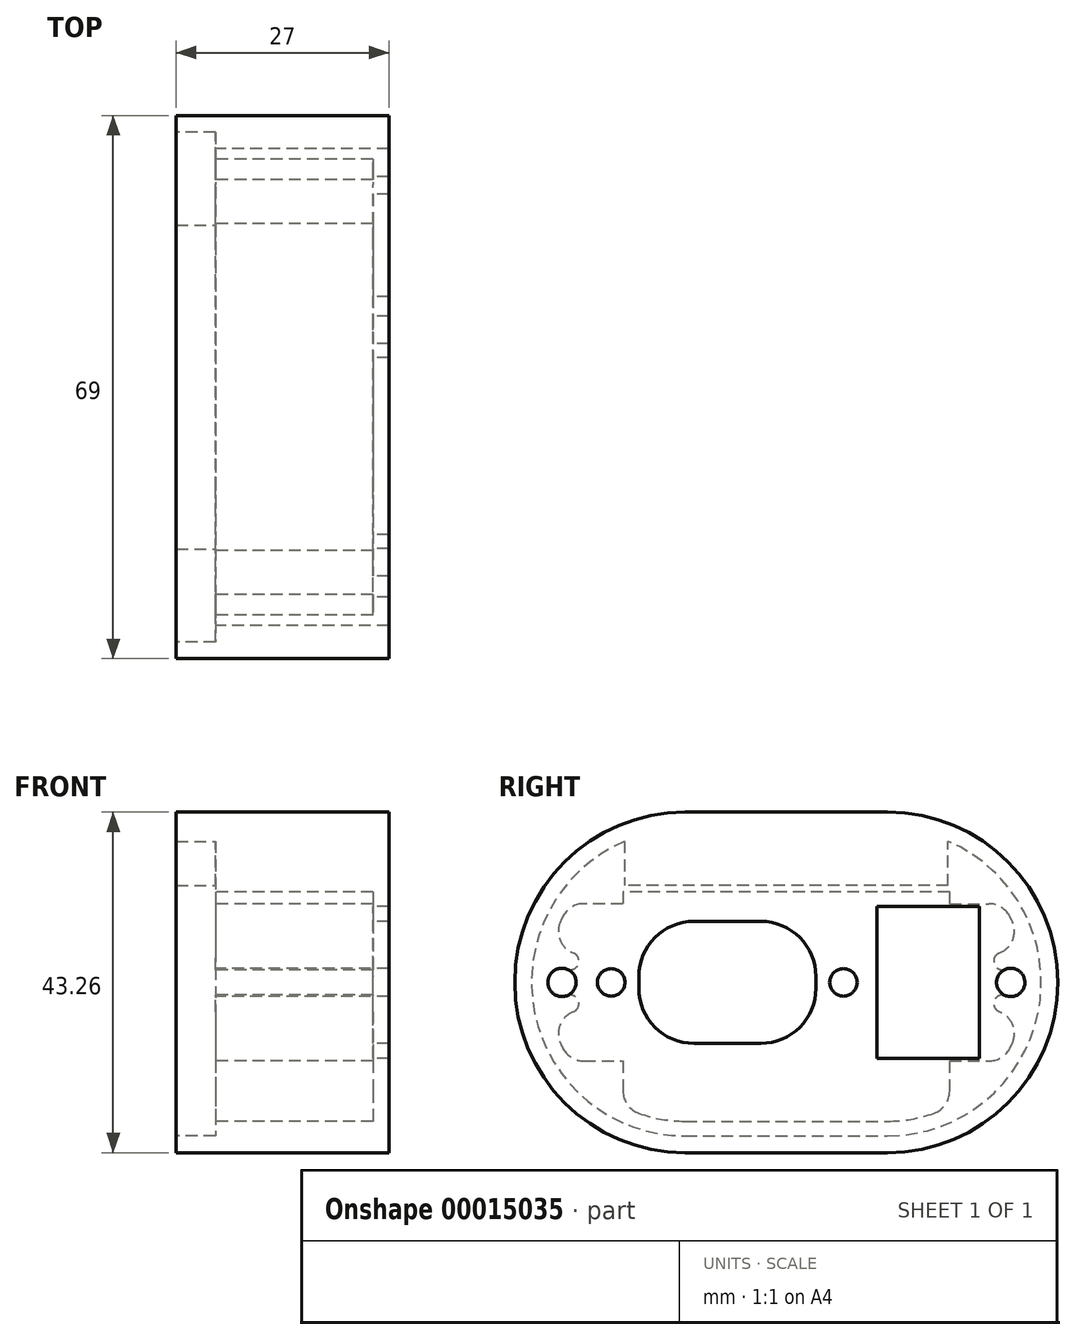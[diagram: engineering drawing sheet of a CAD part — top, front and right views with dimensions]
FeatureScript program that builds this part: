
annotation { "Feature Type Name" : "Feature", "Feature Type Description" : "" }
export const myFeature = defineFeature(function(context is Context, id is Id, definition is map)
    precondition{}
    {
        {
            var Q0;
            Q0=qCreatedBy(makeId("Right.planeOp"),FACE);
            var sketch = newSketch(context, id + "F0", { "sketchPlane" : qUnion([Q0])});
            skLineSegment(sketch, "E0.rect.bottom", {"start": v(23.75, -10) * mm, "end": v(-23.75, -10) * mm});
            skLineSegment(sketch, "E0.rect.top", {"start": v(23.75, 10) * mm, "end": v(-23.75, 10) * mm});
            skLineSegment(sketch, "E0.rect.left", {"start": v(23.75, -10) * mm, "end": v(23.75, 10) * mm});
            skLineSegment(sketch, "E0.rect.right", {"start": v(-23.75, -10) * mm, "end": v(-23.75, 10) * mm});
            skLineSegment(sketch, "E1.bottom", {"start": v(-23.75, 10) * mm, "end": v(23.75, 10) * mm});
            skLineSegment(sketch, "E1.top", {"start": v(-23.75, 12.1) * mm, "end": v(23.75, 12.1) * mm});
            skLineSegment(sketch, "E1.left", {"start": v(-23.75, 10) * mm, "end": v(-23.75, 12.1) * mm});
            skLineSegment(sketch, "E1.right", {"start": v(23.75, 10) * mm, "end": v(23.75, 12.1) * mm});
            skLineSegment(sketch, "E2.bottom", {"start": v(-23.75, -10) * mm, "end": v(23.75, -10) * mm});
            skLineSegment(sketch, "E2.top", {"start": v(-23.75, -12.1) * mm, "end": v(23.75, -12.1) * mm});
            skLineSegment(sketch, "E2.left", {"start": v(-23.75, -10) * mm, "end": v(-23.75, -12.1) * mm});
            skLineSegment(sketch, "E2.right", {"start": v(23.75, -10) * mm, "end": v(23.75, -12.1) * mm});
            skLineSegment(sketch, "E3", {"start": v(-23.75, 10) * mm, "end": v(0, 0) * mm, "construction": true});
            skLineSegment(sketch, "E4", {"start": v(0, 0) * mm, "end": v(23.75, -10) * mm, "construction": true});
            skLineSegment(sketch, "E5", {"start": v(-23.75, -10) * mm, "end": v(-20.75, -10) * mm});
            skLineSegment(sketch, "E6", {"start": v(-20.75, -10) * mm, "end": v(-20.75, -8) * mm});
            skLineSegment(sketch, "E7", {"start": v(-20.75, -8) * mm, "end": v(-25.75, -8) * mm});
            skLineSegment(sketch, "E8", {"start": v(-25.75, -8) * mm, "end": v(-25.75, -14.1) * mm});
            skLineSegment(sketch, "E9", {"start": v(-25.75, -14.1) * mm, "end": v(-20.75, -14.1) * mm});
            skLineSegment(sketch, "E10", {"start": v(-20.75, -14.1) * mm, "end": v(-20.75, -17.1) * mm});
            skLineSegment(sketch, "E11", {"start": v(-20.75, -17.1) * mm, "end": v(20.75, -17.1) * mm});
            skLineSegment(sketch, "E12", {"start": v(20.75, -17.1) * mm, "end": v(20.75, -14.1) * mm});
            skLineSegment(sketch, "E13", {"start": v(20.75, -14.1) * mm, "end": v(25.75, -14.1) * mm});
            skLineSegment(sketch, "E14", {"start": v(25.75, -14.1) * mm, "end": v(25.75, -8) * mm});
            skLineSegment(sketch, "E15", {"start": v(25.75, -8) * mm, "end": v(20.75, -8) * mm});
            skLineSegment(sketch, "E16", {"start": v(20.75, -8) * mm, "end": v(20.75, -10) * mm});
            skLineSegment(sketch, "E17", {"start": v(-20.75, 10) * mm, "end": v(-20.75, 8) * mm});
            skLineSegment(sketch, "E18", {"start": v(-20.75, 8) * mm, "end": v(-25.75, 8) * mm});
            skLineSegment(sketch, "E19", {"start": v(-25.75, 8) * mm, "end": v(-25.75, 14.1) * mm});
            skLineSegment(sketch, "E20", {"start": v(-25.75, 14.1) * mm, "end": v(-20.75, 14.1) * mm});
            skLineSegment(sketch, "E21", {"start": v(-20.75, 14.1) * mm, "end": v(-20.75, 12.1) * mm});
            skLineSegment(sketch, "E22", {"start": v(20.75, 12.1) * mm, "end": v(20.75, 14.1) * mm});
            skLineSegment(sketch, "E23", {"start": v(20.75, 14.1) * mm, "end": v(25.75, 14.1) * mm});
            skLineSegment(sketch, "E24", {"start": v(25.75, 14.1) * mm, "end": v(25.75, 8) * mm});
            skLineSegment(sketch, "E25", {"start": v(25.75, 8) * mm, "end": v(20.75, 8) * mm});
            skLineSegment(sketch, "E26", {"start": v(20.75, 8) * mm, "end": v(20.75, 10) * mm});
            skCircle(sketch, "E27", {"center": v(-28.5, 0) * mm, "radius": 1.25 * mm});
            skCircle(sketch, "E28", {"center": v(28.5, 0) * mm, "radius": 1.25 * mm});
            skLineSegment(sketch, "E29", {"start": v(-28.5, 0) * mm, "end": v(0, 0) * mm, "construction": true});
            skLineSegment(sketch, "E30", {"start": v(28.5, 0) * mm, "end": v(0, 0) * mm, "construction": true});
            skLineSegment(sketch, "E31.bottom", {"start": v(-25.75, -14.1) * mm, "end": v(25.75, -14.1) * mm});
            skLineSegment(sketch, "E31.top", {"start": v(-25.75, -19.1) * mm, "end": v(25.75, -19.1) * mm});
            skLineSegment(sketch, "E31.left", {"start": v(-25.75, -14.1) * mm, "end": v(-25.75, -19.1) * mm});
            skLineSegment(sketch, "E31.right", {"start": v(25.75, -14.1) * mm, "end": v(25.75, -19.1) * mm});
            skArc(sketch, "E32", {"start": v(-12.87, 19.1) * mm, "mid": v(-31.97, 0) * mm, "end": v(-12.87, -19.1) * mm});
            skArc(sketch, "E33", {"start": v(12.87, -19.1) * mm, "mid": v(31.97, 0) * mm, "end": v(12.87, 19.1) * mm});
            skLineSegment(sketch, "E34", {"start": v(-12.87, 19.1) * mm, "end": v(-12.87, 0) * mm, "construction": true});
            skLineSegment(sketch, "E35", {"start": v(-12.87, -19.1) * mm, "end": v(-12.87, 0) * mm, "construction": true});
            skLineSegment(sketch, "E36", {"start": v(12.87, 0) * mm, "end": v(12.87, 19.1) * mm, "construction": true});
            skLineSegment(sketch, "E37", {"start": v(12.87, 0) * mm, "end": v(12.87, -19.1) * mm, "construction": true});
            skLineSegment(sketch, "E38.rect.bottom", {"start": v(24.5, -9.65) * mm, "end": v(11.5, -9.65) * mm});
            skLineSegment(sketch, "E38.rect.top", {"start": v(24.5, 9.65) * mm, "end": v(11.5, 9.65) * mm});
            skLineSegment(sketch, "E38.rect.left", {"start": v(24.5, -9.65) * mm, "end": v(24.5, 9.65) * mm});
            skLineSegment(sketch, "E38.rect.right", {"start": v(11.5, -9.65) * mm, "end": v(11.5, 9.65) * mm});
            skPoint(sketch, "E38.rect.middle", {"position": v(18, 0) * mm});
            skLineSegment(sketch, "E39.rect.bottom", {"start": v(3.75, -7.75) * mm, "end": v(-18.75, -7.75) * mm});
            skLineSegment(sketch, "E39.rect.top", {"start": v(3.75, 7.75) * mm, "end": v(-18.75, 7.75) * mm});
            skLineSegment(sketch, "E39.rect.left", {"start": v(3.75, -7.75) * mm, "end": v(3.75, 7.75) * mm});
            skLineSegment(sketch, "E39.rect.right", {"start": v(-18.75, -7.75) * mm, "end": v(-18.75, 7.75) * mm});
            skPoint(sketch, "E39.rect.middle", {"position": v(-7.5, 0) * mm});
            skCircle(sketch, "E40", {"center": v(-22.25, 0) * mm, "radius": 1.75 * mm});
            skCircle(sketch, "E41", {"center": v(7.25, 0) * mm, "radius": 1.75 * mm});
            skLineSegment(sketch, "E42", {"start": v(-22.25, 0) * mm, "end": v(-7.5, 0) * mm, "construction": true});
            skLineSegment(sketch, "E43", {"start": v(-7.5, 0) * mm, "end": v(7.25, 0) * mm, "construction": true});
            skLineSegment(sketch, "E44.rect.bottom", {"start": v(10.5, 8.5) * mm, "end": v(-25.5, 8.5) * mm});
            skLineSegment(sketch, "E44.rect.top", {"start": v(10.5, -8.5) * mm, "end": v(-25.5, -8.5) * mm});
            skLineSegment(sketch, "E44.rect.left", {"start": v(10.5, 8.5) * mm, "end": v(10.5, -8.5) * mm});
            skLineSegment(sketch, "E44.rect.right", {"start": v(-25.5, 8.5) * mm, "end": v(-25.5, -8.5) * mm});
            skLineSegment(sketch, "E45.rect.bottom", {"start": v(25.5, 10.5) * mm, "end": v(10.5, 10.5) * mm});
            skLineSegment(sketch, "E45.rect.top", {"start": v(25.5, -10.5) * mm, "end": v(10.5, -10.5) * mm});
            skLineSegment(sketch, "E45.rect.left", {"start": v(25.5, 10.5) * mm, "end": v(25.5, -10.5) * mm});
            skLineSegment(sketch, "E45.rect.right", {"start": v(10.5, 10.5) * mm, "end": v(10.5, -10.5) * mm});
            skLineSegment(sketch, "E46", {"start": v(-20.75, 14.1) * mm, "end": v(-20.75, 17.4) * mm});
            skLineSegment(sketch, "E47", {"start": v(20.75, 14.1) * mm, "end": v(20.75, 17.4) * mm});
            skSolve(sketch);
        }
        {
            var Q0;
            Q0=qCreatedBy(makeId("Right.planeOp"),FACE);
            var sketch = newSketch(context, id + "F1", { "sketchPlane" : qUnion([Q0])});
            skArc(sketch, "E48", {"start": v(-12.87, 19.5) * mm, "mid": v(-32.37, 0) * mm, "end": v(-12.87, -19.5) * mm});
            skArc(sketch, "E49", {"start": v(12.87, -19.5) * mm, "mid": v(32.37, 0) * mm, "end": v(12.87, 19.5) * mm});
            skLineSegment(sketch, "E50", {"start": v(-12.87, 19.5) * mm, "end": v(12.87, 19.5) * mm});
            skLineSegment(sketch, "E51", {"start": v(-12.87, -19.5) * mm, "end": v(12.87, -19.5) * mm});
            skLineSegment(sketch, "E52.0", {"start": v(-12.87, 21.63) * mm, "end": v(12.87, 21.63) * mm});
            skArc(sketch, "E52.1", {"start": v(-12.87, 21.63) * mm, "mid": v(-34.5, 0) * mm, "end": v(-12.87, -21.63) * mm});
            skLineSegment(sketch, "E52.2", {"start": v(-12.87, -21.63) * mm, "end": v(12.87, -21.63) * mm});
            skArc(sketch, "E52.3", {"start": v(12.87, -21.63) * mm, "mid": v(34.5, 0) * mm, "end": v(12.87, 21.63) * mm});
            skPoint(sketch, "E53", {"position": v(-34.5, 0) * mm});
            skPoint(sketch, "E54", {"position": v(34.5, 0) * mm});
            skSolve(sketch);
        }
        {
            var Q0;
            Q0 = qSketchRegion(id + "F1", true);
            extrude(context, id + "F2", {"entities" : qUnion([Q0]), "depth" : 5 * mm});
        }
        {
            var Q0;
            Q0=makeQuery(id+"F2.opExtrude","CAP_FACE",FACE,{"disambiguationData":[OSD([sQuery(id+"F1.wireOp",EDGE,"E48"),sQuery(id+"F1.wireOp",EDGE,"E49"),sQuery(id+"F1.wireOp",EDGE,"E50"),sQuery(id+"F1.wireOp",EDGE,"E51"),sQuery(id+"F1.wireOp",EDGE,"E52.0"),sQuery(id+"F1.wireOp",EDGE,"E52.1"),sQuery(id+"F1.wireOp",EDGE,"E52.2"),sQuery(id+"F1.wireOp",EDGE,"E52.3")])],"isStart":false});
            var sketch = newSketch(context, id + "F3", { "sketchPlane" : qUnion([Q0])});
            skLineSegment(sketch, "E55.0", {"start": v(-12.87, 17.63) * mm, "end": v(12.87, 17.63) * mm, "construction": true});
            skArc(sketch, "E55.1", {"start": v(-12.87, 17.63) * mm, "mid": v(-15.85, 17.38) * mm, "end": v(-18.75, 16.62) * mm, "construction": true});
            skLineSegment(sketch, "E55.2", {"start": v(-12.87, -17.63) * mm, "end": v(12.87, -17.63) * mm});
            skArc(sketch, "E55.3", {"start": v(12.87, -17.63) * mm, "mid": v(15.85, -17.38) * mm, "end": v(18.75, -16.62) * mm});
            skLineSegment(sketch, "E56.0", {"start": v(-12.87, 21.63) * mm, "end": v(12.87, 21.63) * mm});
            skArc(sketch, "E56.1", {"start": v(-12.87, 21.63) * mm, "mid": v(-34.5, 0) * mm, "end": v(-12.87, -21.63) * mm});
            skArc(sketch, "E56.2", {"start": v(12.87, -21.63) * mm, "mid": v(34.5, 0) * mm, "end": v(12.87, 21.63) * mm});
            skLineSegment(sketch, "E56.3", {"start": v(-12.87, -21.63) * mm, "end": v(12.87, -21.63) * mm});
            skArc(sketch, "E57", {"start": v(-27.85, 1.68) * mm, "mid": v(-30.3, 0) * mm, "end": v(-27.85, -1.68) * mm});
            skArc(sketch, "E58", {"start": v(27.85, -1.68) * mm, "mid": v(30.3, 0) * mm, "end": v(27.85, 1.68) * mm});
            skArc(sketch, "E59", {"start": v(27.05, 3.73) * mm, "mid": v(24.5, 0) * mm, "end": v(27.05, -3.73) * mm, "construction": true});
            skArc(sketch, "E60.trimOffspring", {"start": v(-28.65, -7.86) * mm, "mid": v(-28.5, -8.15) * mm, "end": v(-28.35, -8.44) * mm});
            skArc(sketch, "E61.trimOffspring", {"start": v(28.65, 7.86) * mm, "mid": v(28.5, 8.15) * mm, "end": v(28.35, 8.44) * mm});
            skPoint(sketch, "E62.visualSharp", {"position": v(-28.65, 7.86) * mm});
            skArc(sketch, "E62.filletArc", {"start": v(-28.65, 7.86) * mm, "mid": v(-28.76, 5.44) * mm, "end": v(-27.05, 3.73) * mm});
            skArc(sketch, "E63.filletArc", {"start": v(-27.05, -3.73) * mm, "mid": v(-28.76, -5.44) * mm, "end": v(-28.65, -7.86) * mm});
            skPoint(sketch, "E64.visualSharp", {"position": v(30.12, 3.66) * mm});
            skArc(sketch, "E64.filletArc", {"start": v(27.05, 3.73) * mm, "mid": v(28.76, 5.44) * mm, "end": v(28.65, 7.86) * mm});
            skPoint(sketch, "E65.visualSharp", {"position": v(30.12, -3.66) * mm});
            skArc(sketch, "E65.filletArc", {"start": v(28.65, -7.86) * mm, "mid": v(28.76, -5.44) * mm, "end": v(27.05, -3.73) * mm});
            skArc(sketch, "E66", {"start": v(-27.85, 1.68) * mm, "mid": v(-26.42, 2.3) * mm, "end": v(-27.05, 3.73) * mm});
            skArc(sketch, "E67", {"start": v(-27.05, -3.73) * mm, "mid": v(-26.42, -2.3) * mm, "end": v(-27.85, -1.68) * mm});
            skArc(sketch, "E68", {"start": v(27.05, 3.73) * mm, "mid": v(26.42, 2.3) * mm, "end": v(27.85, 1.68) * mm});
            skArc(sketch, "E69", {"start": v(27.85, -1.68) * mm, "mid": v(26.42, -2.3) * mm, "end": v(27.05, -3.73) * mm});
            skCircle(sketch, "E70", {"center": v(-28.5, 0) * mm, "radius": 1.8 * mm, "construction": true});
            skCircle(sketch, "E71", {"center": v(-28.5, 0) * mm, "radius": 4 * mm, "construction": true});
            skLineSegment(sketch, "E72", {"start": v(20.75, 13.8) * mm, "end": v(20.75, 10) * mm, "construction": true});
            skLineSegment(sketch, "E73", {"start": v(20.75, 10) * mm, "end": v(25.72, 10) * mm});
            skLineSegment(sketch, "E74", {"start": v(-20.75, 13.8) * mm, "end": v(-20.75, 10) * mm, "construction": true});
            skLineSegment(sketch, "E75", {"start": v(-20.75, 10) * mm, "end": v(-25.72, 10) * mm});
            skLineSegment(sketch, "E76", {"start": v(-25.72, -10) * mm, "end": v(-20.75, -10) * mm});
            skLineSegment(sketch, "E77", {"start": v(-20.75, -10) * mm, "end": v(-20.75, -13.8) * mm});
            skLineSegment(sketch, "E78", {"start": v(20.75, -13.8) * mm, "end": v(20.75, -10) * mm});
            skLineSegment(sketch, "E79", {"start": v(20.75, -10) * mm, "end": v(25.72, -10) * mm});
            skArc(sketch, "E80.trimOffspring", {"start": v(-28.35, 8.44) * mm, "mid": v(-28.5, 8.15) * mm, "end": v(-28.65, 7.86) * mm});
            skArc(sketch, "E81.trimOffspring", {"start": v(18.75, 16.62) * mm, "mid": v(15.85, 17.38) * mm, "end": v(12.87, 17.63) * mm, "construction": true});
            skArc(sketch, "E82.trimOffspring", {"start": v(28.35, -8.44) * mm, "mid": v(28.5, -8.15) * mm, "end": v(28.65, -7.86) * mm});
            skArc(sketch, "E83.trimOffspring", {"start": v(-18.75, -16.62) * mm, "mid": v(-15.85, -17.38) * mm, "end": v(-12.87, -17.63) * mm});
            skPoint(sketch, "E84.visualSharp", {"position": v(-20.75, 15.77) * mm});
            skArc(sketch, "E84.filletArc", {"start": v(-18.75, 16.62) * mm, "mid": v(-20.2, 15.53) * mm, "end": v(-20.75, 13.8) * mm, "construction": true});
            skPoint(sketch, "E85.visualSharp", {"position": v(-27.4, 10) * mm});
            skArc(sketch, "E85.filletArc", {"start": v(-25.72, 10) * mm, "mid": v(-27.25, 9.58) * mm, "end": v(-28.35, 8.44) * mm});
            skPoint(sketch, "E86.visualSharp", {"position": v(-27.4, -10) * mm});
            skArc(sketch, "E86.filletArc", {"start": v(-28.35, -8.44) * mm, "mid": v(-27.25, -9.58) * mm, "end": v(-25.72, -10) * mm});
            skPoint(sketch, "E87.visualSharp", {"position": v(-20.75, -15.77) * mm});
            skArc(sketch, "E87.filletArc", {"start": v(-20.75, -13.8) * mm, "mid": v(-20.2, -15.53) * mm, "end": v(-18.75, -16.62) * mm});
            skPoint(sketch, "E88.visualSharp", {"position": v(20.75, -15.77) * mm});
            skArc(sketch, "E88.filletArc", {"start": v(18.75, -16.62) * mm, "mid": v(20.2, -15.53) * mm, "end": v(20.75, -13.8) * mm});
            skPoint(sketch, "E89.visualSharp", {"position": v(27.4, -10) * mm});
            skArc(sketch, "E89.filletArc", {"start": v(25.72, -10) * mm, "mid": v(27.25, -9.58) * mm, "end": v(28.35, -8.44) * mm});
            skPoint(sketch, "E90.visualSharp", {"position": v(27.4, 10) * mm});
            skArc(sketch, "E90.filletArc", {"start": v(28.35, 8.44) * mm, "mid": v(27.25, 9.58) * mm, "end": v(25.72, 10) * mm});
            skPoint(sketch, "E91.visualSharp", {"position": v(20.75, 15.77) * mm});
            skArc(sketch, "E91.filletArc", {"start": v(20.75, 13.8) * mm, "mid": v(20.2, 15.53) * mm, "end": v(18.75, 16.62) * mm, "construction": true});
            skLineSegment(sketch, "E92", {"start": v(20.75, 11.5) * mm, "end": v(-20.75, 11.5) * mm});
            skLineSegment(sketch, "E93", {"start": v(-20.75, 11.5) * mm, "end": v(-20.75, 10) * mm});
            skLineSegment(sketch, "E94", {"start": v(20.75, 10) * mm, "end": v(20.75, 11.5) * mm});
            skSolve(sketch);
        }
        {
            var Q0;
            Q0 = qSketchRegion(id + "F3", true);
            extrude(context, id + "F4", {"entities" : qUnion([Q0]), "operationType" : NewBodyOperationType.ADD, "depth" : 20 * mm});
        }
        {
            var Q0;
            Q0=makeQuery(id+"F4.opExtrude","CAP_FACE",FACE,{"disambiguationData":[OSD([sQuery(id+"F3.wireOp",EDGE,"E55.0"),sQuery(id+"F3.wireOp",EDGE,"E55.1"),sQuery(id+"F3.wireOp",EDGE,"E55.2"),sQuery(id+"F3.wireOp",EDGE,"E55.3"),sQuery(id+"F3.wireOp",EDGE,"E56.0"),sQuery(id+"F3.wireOp",EDGE,"E56.1"),sQuery(id+"F3.wireOp",EDGE,"E56.2"),sQuery(id+"F3.wireOp",EDGE,"E56.3"),sQuery(id+"F3.wireOp",EDGE,"E57"),sQuery(id+"F3.wireOp",EDGE,"E58"),sQuery(id+"F3.wireOp",EDGE,"E60.trimOffspring"),sQuery(id+"F3.wireOp",EDGE,"E61.trimOffspring"),sQuery(id+"F3.wireOp",EDGE,"E62.filletArc"),sQuery(id+"F3.wireOp",EDGE,"E63.filletArc"),sQuery(id+"F3.wireOp",EDGE,"E64.filletArc"),sQuery(id+"F3.wireOp",EDGE,"E65.filletArc"),sQuery(id+"F3.wireOp",EDGE,"E66"),sQuery(id+"F3.wireOp",EDGE,"E67"),sQuery(id+"F3.wireOp",EDGE,"E68"),sQuery(id+"F3.wireOp",EDGE,"E69")])],"isStart":false});
            var sketch = newSketch(context, id + "F5", { "sketchPlane" : qUnion([Q0])});
            skLineSegment(sketch, "E95.0", {"start": v(-12.87, 21.63) * mm, "end": v(12.87, 21.63) * mm});
            skArc(sketch, "E95.1", {"start": v(-12.87, 21.63) * mm, "mid": v(-34.5, 0) * mm, "end": v(-12.87, -21.63) * mm});
            skLineSegment(sketch, "E95.2", {"start": v(-12.87, -21.63) * mm, "end": v(12.87, -21.63) * mm});
            skArc(sketch, "E95.3", {"start": v(12.87, -21.63) * mm, "mid": v(34.5, 0) * mm, "end": v(12.87, 21.63) * mm});
            skCircle(sketch, "E96.0", {"center": v(-22.25, 0) * mm, "radius": 1.75 * mm});
            skCircle(sketch, "E96.1", {"center": v(7.25, 0) * mm, "radius": 1.75 * mm});
            skLineSegment(sketch, "E97.0", {"start": v(-18.75, -0.75) * mm, "end": v(-18.75, 0.75) * mm});
            skLineSegment(sketch, "E97.1", {"start": v(-3.25, 7.75) * mm, "end": v(-11.75, 7.75) * mm});
            skLineSegment(sketch, "E97.2", {"start": v(3.75, -0.75) * mm, "end": v(3.75, 0.75) * mm});
            skLineSegment(sketch, "E97.3", {"start": v(-3.25, -7.75) * mm, "end": v(-11.75, -7.75) * mm});
            skLineSegment(sketch, "E98.0", {"start": v(11.5, -9.65) * mm, "end": v(11.5, 9.65) * mm});
            skLineSegment(sketch, "E98.1", {"start": v(24.5, 9.65) * mm, "end": v(11.5, 9.65) * mm});
            skLineSegment(sketch, "E98.2", {"start": v(24.5, -9.65) * mm, "end": v(24.5, 9.65) * mm});
            skLineSegment(sketch, "E98.3", {"start": v(24.5, -9.65) * mm, "end": v(11.5, -9.65) * mm});
            skPoint(sketch, "E99.visualSharp", {"position": v(-18.75, 7.75) * mm});
            skArc(sketch, "E99.filletArc", {"start": v(-11.75, 7.75) * mm, "mid": v(-16.7, 5.7) * mm, "end": v(-18.75, 0.75) * mm});
            skPoint(sketch, "E100.visualSharp", {"position": v(-18.75, -7.75) * mm});
            skArc(sketch, "E100.filletArc", {"start": v(-18.75, -0.75) * mm, "mid": v(-16.7, -5.7) * mm, "end": v(-11.75, -7.75) * mm});
            skPoint(sketch, "E101.visualSharp", {"position": v(3.75, 7.75) * mm});
            skArc(sketch, "E101.filletArc", {"start": v(3.75, 0.75) * mm, "mid": v(1.7, 5.7) * mm, "end": v(-3.25, 7.75) * mm});
            skPoint(sketch, "E102.visualSharp", {"position": v(3.75, -7.75) * mm});
            skArc(sketch, "E102.filletArc", {"start": v(-3.25, -7.75) * mm, "mid": v(1.7, -5.7) * mm, "end": v(3.75, -0.75) * mm});
            skCircle(sketch, "E103", {"center": v(-28.5, 0) * mm, "radius": 1.8 * mm});
            skCircle(sketch, "E104", {"center": v(28.5, 0) * mm, "radius": 1.8 * mm});
            skSolve(sketch);
        }
        {
            var Q0;
            Q0 = qSketchRegion(id + "F5", true);
            extrude(context, id + "F6", {"entities" : qUnion([Q0]), "operationType" : NewBodyOperationType.ADD, "depth" : 2 * mm});
        }
        {
            var Q0;
            Q0=makeQuery(id+"F4.opExtrude","CAP_FACE",FACE,{"disambiguationData":[OSD([sQuery(id+"F3.wireOp",EDGE,"E55.2"),sQuery(id+"F3.wireOp",EDGE,"E55.3"),sQuery(id+"F3.wireOp",EDGE,"E56.0"),sQuery(id+"F3.wireOp",EDGE,"E56.1"),sQuery(id+"F3.wireOp",EDGE,"E56.2"),sQuery(id+"F3.wireOp",EDGE,"E56.3"),sQuery(id+"F3.wireOp",EDGE,"E57"),sQuery(id+"F3.wireOp",EDGE,"E58"),sQuery(id+"F3.wireOp",EDGE,"E60.trimOffspring"),sQuery(id+"F3.wireOp",EDGE,"E61.trimOffspring"),sQuery(id+"F3.wireOp",EDGE,"E62.filletArc"),sQuery(id+"F3.wireOp",EDGE,"E63.filletArc"),sQuery(id+"F3.wireOp",EDGE,"E64.filletArc"),sQuery(id+"F3.wireOp",EDGE,"E65.filletArc"),sQuery(id+"F3.wireOp",EDGE,"E66"),sQuery(id+"F3.wireOp",EDGE,"E67"),sQuery(id+"F3.wireOp",EDGE,"E68"),sQuery(id+"F3.wireOp",EDGE,"E69"),sQuery(id+"F3.wireOp",EDGE,"E73"),sQuery(id+"F3.wireOp",EDGE,"E75"),sQuery(id+"F3.wireOp",EDGE,"E76"),sQuery(id+"F3.wireOp",EDGE,"E77"),sQuery(id+"F3.wireOp",EDGE,"E78"),sQuery(id+"F3.wireOp",EDGE,"E79"),sQuery(id+"F3.wireOp",EDGE,"E80.trimOffspring"),sQuery(id+"F3.wireOp",EDGE,"E82.trimOffspring"),sQuery(id+"F3.wireOp",EDGE,"E83.trimOffspring"),sQuery(id+"F3.wireOp",EDGE,"E85.filletArc"),sQuery(id+"F3.wireOp",EDGE,"E86.filletArc"),sQuery(id+"F3.wireOp",EDGE,"E87.filletArc"),sQuery(id+"F3.wireOp",EDGE,"E88.filletArc"),sQuery(id+"F3.wireOp",EDGE,"E89.filletArc"),sQuery(id+"F3.wireOp",EDGE,"E90.filletArc"),sQuery(id+"F3.wireOp",EDGE,"E92"),sQuery(id+"F3.wireOp",EDGE,"E93"),sQuery(id+"F3.wireOp",EDGE,"E94")])],"isStart":true});
            var sketch = newSketch(context, id + "F7", { "sketchPlane" : qUnion([Q0])});
            skLineSegment(sketch, "E105", {"start": v(-20.55, 12.3) * mm, "end": v(-20.55, 17.92) * mm});
            skArc(sketch, "E106.0", {"start": v(-20.55, 17.92) * mm, "mid": v(-16.79, 19.1) * mm, "end": v(-12.87, 19.5) * mm});
            skLineSegment(sketch, "E106.1", {"start": v(12.87, 19.5) * mm, "end": v(-12.87, 19.5) * mm});
            skArc(sketch, "E106.2", {"start": v(12.87, 19.5) * mm, "mid": v(16.79, 19.1) * mm, "end": v(20.55, 17.92) * mm});
            skPoint(sketch, "E107.orphan", {"position": v(-12.87, -19.5) * mm});
            skLineSegment(sketch, "E108", {"start": v(20.55, 17.92) * mm, "end": v(20.55, 12.3) * mm});
            skPoint(sketch, "E109.orphan", {"position": v(12.87, -19.5) * mm});
            skLineSegment(sketch, "E110", {"start": v(-20.55, 12.3) * mm, "end": v(20.55, 12.3) * mm});
            skSolve(sketch);
        }
        {
            var Q0;
            Q0 = qSketchRegion(id + "F7", true);
            extrude(context, id + "F8", {"entities" : qUnion([Q0]), "operationType" : NewBodyOperationType.ADD, "depth" : 5 * mm});
        }
    });
